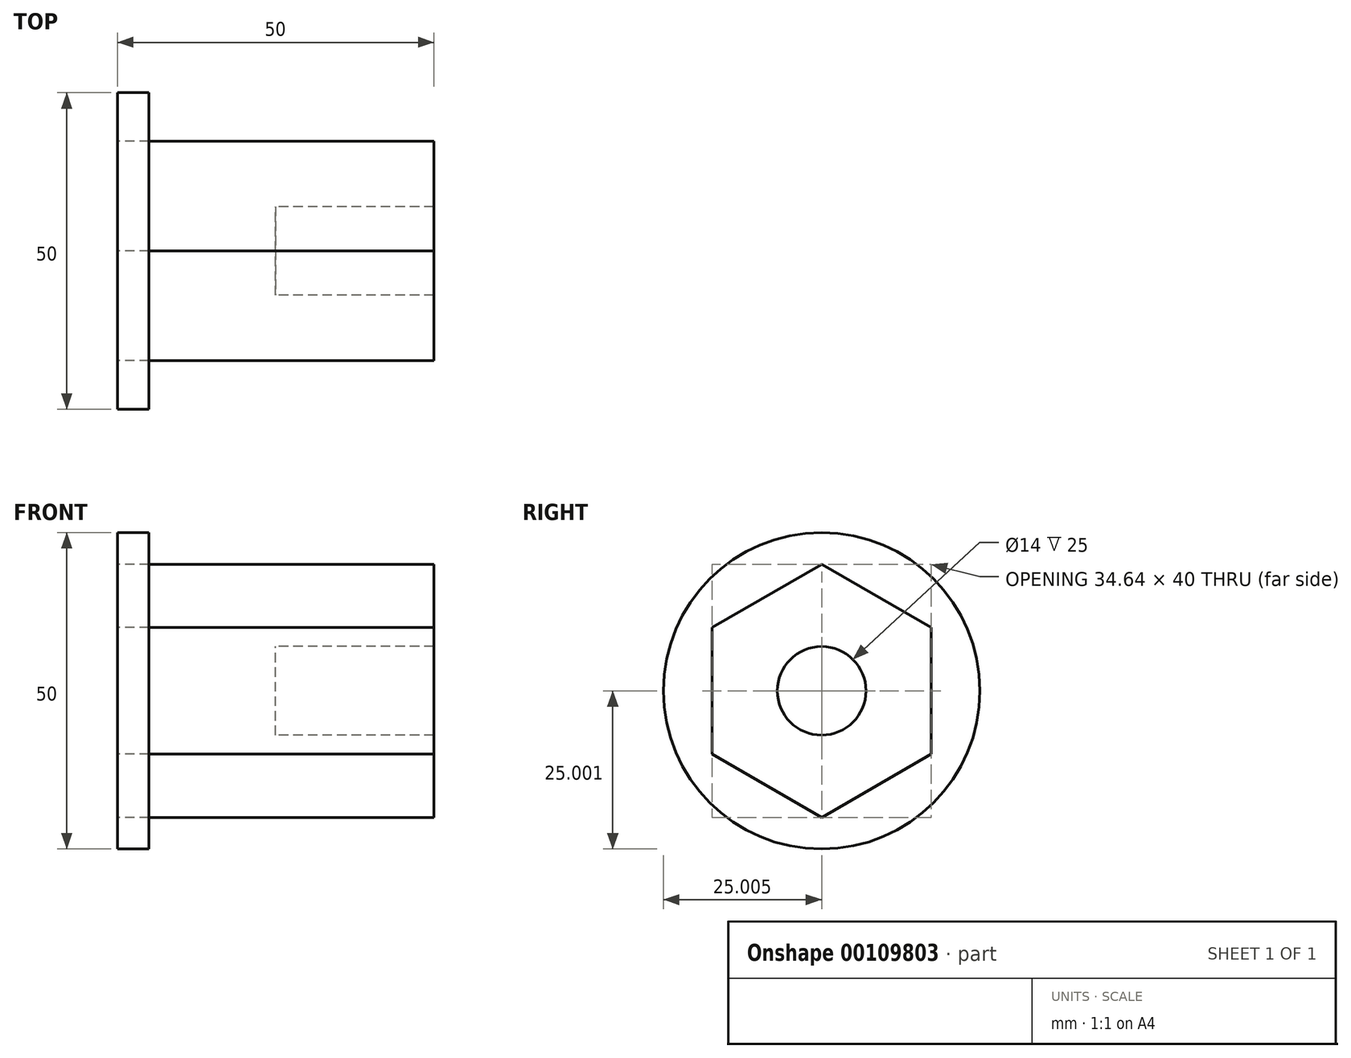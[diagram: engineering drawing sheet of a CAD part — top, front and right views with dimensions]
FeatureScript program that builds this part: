
annotation { "Feature Type Name" : "Feature", "Feature Type Description" : "" }
export const myFeature = defineFeature(function(context is Context, id is Id, definition is map)
    precondition{}
    {
        {
            var Q0;
            Q0=qCreatedBy(makeId("Right.planeOp"),FACE);
            var sketch = newSketch(context, id + "F0", { "sketchPlane" : qUnion([Q0])});
            skLineSegment(sketch, "E0", {"start": v(-258.27, -19.33) * mm, "end": v(-8.74, -19.33) * mm});
            skLineSegment(sketch, "E1", {"start": v(11.1, 3.15) * mm, "end": v(-12.25, 190) * mm});
            skLineSegment(sketch, "E2", {"start": v(-12.25, 190) * mm, "end": v(327.44, 461.76) * mm});
            skLineSegment(sketch, "E3", {"start": v(-148.68, -349.33) * mm, "end": v(-630.63, -349.33) * mm});
            skLineSegment(sketch, "E4", {"start": v(-18.68, -199.33) * mm, "end": v(-121.84, -199.33) * mm});
            skLineSegment(sketch, "E5", {"start": v(11.58, 180.67) * mm, "end": v(241.26, 180.67) * mm});
            skLineSegment(sketch, "E6", {"start": v(261.1, 203.15) * mm, "end": v(241.73, 358.2) * mm});
            skLineSegment(sketch, "E7", {"start": v(261.58, 380.67) * mm, "end": v(392.26, 380.67) * mm});
            skLineSegment(sketch, "E8", {"start": v(-148.68, -189.33) * mm, "end": v(-148.68, -349.33) * mm});
            skLineSegment(sketch, "E9", {"start": v(-290, -189.33) * mm, "end": v(-290, -119.33) * mm});
            skLineSegment(sketch, "E10", {"start": v(-121.84, -169.33) * mm, "end": v(-258.27, -169.33) * mm});
            skLineSegment(sketch, "E11", {"start": v(-148.68, -189.33) * mm, "end": v(-290, -189.33) * mm});
            skLineSegment(sketch, "E12", {"start": v(-258.27, -169.33) * mm, "end": v(-258.27, -19.33) * mm});
            skLineSegment(sketch, "E13", {"start": v(260.59, 545.38) * mm, "end": v(630.63, 82.5) * mm});
            skLineSegment(sketch, "E14", {"start": v(-630.63, 87.12) * mm, "end": v(-630.63, -443.05) * mm});
            skArc(sketch, "E15", {"start": v(-8.74, -19.33) * mm, "mid": v(6.26, -12.56) * mm, "end": v(11.1, 3.15) * mm});
            skArc(sketch, "E16", {"start": v(11.58, 180.67) * mm, "mid": v(-3.42, 173.9) * mm, "end": v(-8.27, 158.2) * mm});
            skArc(sketch, "E17", {"start": v(241.26, 180.67) * mm, "mid": v(256.26, 187.44) * mm, "end": v(261.1, 203.15) * mm});
            skArc(sketch, "E18", {"start": v(261.58, 380.67) * mm, "mid": v(246.58, 373.9) * mm, "end": v(241.73, 358.2) * mm});
            skLineSegment(sketch, "E19", {"start": v(-148.68, -349.33) * mm, "end": v(592.58, -349.33) * mm});
            skLineSegment(sketch, "E20", {"start": v(168.82, -49.33) * mm, "end": v(592.58, -49.33) * mm});
            skLineSegment(sketch, "E21", {"start": v(592.58, 18.95) * mm, "end": v(592.58, -393.06) * mm});
            skLineSegment(sketch, "E22", {"start": v(-18.68, -199.33) * mm, "end": v(514.77, 227.43) * mm});
            skLineSegment(sketch, "E23", {"start": v(-148.68, -299.33) * mm, "end": v(-630.63, -299.33) * mm});
            skLineSegment(sketch, "E24", {"start": v(-121.84, -199.33) * mm, "end": v(-121.84, -169.33) * mm});
            skLineSegment(sketch, "E25", {"start": v(-290, -119.33) * mm, "end": v(-630.63, -119.33) * mm});
            skLineSegment(sketch, "E26", {"start": v(-258.27, -19.33) * mm, "end": v(-630.63, -19.33) * mm});
            skLineSegment(sketch, "E27", {"start": v(-258.27, -169.33) * mm, "end": v(-258.27, -189.33) * mm});
            skLineSegment(sketch, "E28", {"start": v(-148.68, -189.33) * mm, "end": v(-148.68, -169.33) * mm});
            skLineSegment(sketch, "E29", {"start": v(-258.27, -169.33) * mm, "end": v(-148.68, -189.33) * mm});
            skLineSegment(sketch, "E30", {"start": v(-148.68, -169.33) * mm, "end": v(-258.27, -189.33) * mm});
            skArc(sketch, "E31", {"start": v(-132.68, -239.33) * mm, "mid": v(-128.58, -229.43) * mm, "end": v(-118.68, -225.33) * mm});
            skLineSegment(sketch, "E32", {"start": v(-118.68, -225.33) * mm, "end": v(-25.68, -225.33) * mm});
            skArc(sketch, "E33", {"start": v(-25.68, -225.33) * mm, "mid": v(-20.73, -223.28) * mm, "end": v(-18.68, -218.33) * mm});
            skLineSegment(sketch, "E34", {"start": v(-18.68, -218.33) * mm, "end": v(-18.68, -209.33) * mm});
            skLineSegment(sketch, "E35", {"start": v(-18.68, -209.33) * mm, "end": v(-148.68, -209.33) * mm});
            skLineSegment(sketch, "E36", {"start": v(-148.68, -209.33) * mm, "end": v(-148.68, -339.33) * mm});
            skLineSegment(sketch, "E37", {"start": v(-148.68, -339.33) * mm, "end": v(-139.68, -339.33) * mm});
            skArc(sketch, "E38", {"start": v(-139.68, -339.33) * mm, "mid": v(-134.73, -337.28) * mm, "end": v(-132.68, -332.33) * mm});
            skLineSegment(sketch, "E39", {"start": v(-132.68, -332.33) * mm, "end": v(-132.68, -239.33) * mm});
            skLineSegment(sketch, "E40", {"start": v(122.07, -484.72) * mm, "end": v(142.07, -484.72) * mm});
            skLineSegment(sketch, "E41", {"start": v(142.07, -484.72) * mm, "end": v(142.07, -524.72) * mm});
            skLineSegment(sketch, "E42", {"start": v(142.07, -524.72) * mm, "end": v(122.07, -524.72) * mm});
            skLineSegment(sketch, "E43", {"start": v(122.07, -524.72) * mm, "end": v(122.07, -484.72) * mm});
            skLineSegment(sketch, "E44", {"start": v(122.07, -494.72) * mm, "end": v(142.07, -494.72) * mm});
            skLineSegment(sketch, "E45", {"start": v(122.07, -514.72) * mm, "end": v(142.07, -514.72) * mm});
            skEllipse(sketch, "E46", {"center": v(132.07, -489.72) * mm, "majorRadius": 10 * mm, "minorRadius": 5 * mm, "majorAxis": v(-1, 0)});
            skEllipse(sketch, "E47", {"center": v(132.07, -519.72) * mm, "majorRadius": 10 * mm, "minorRadius": 5 * mm, "majorAxis": v(-1, 0)});
            skEllipse(sketch, "E48", {"center": v(132.07, -504.72) * mm, "majorRadius": 10 * mm, "minorRadius": 10 * mm, "majorAxis": v(0, 1)});
            skLineSegment(sketch, "E49", {"start": v(142.07, -497.72) * mm, "end": v(148.92, -497.72) * mm});
            skLineSegment(sketch, "E50", {"start": v(142.07, -511.72) * mm, "end": v(148.92, -511.72) * mm});
            skLineSegment(sketch, "E51", {"start": v(148.92, -497.72) * mm, "end": v(148.92, -511.72) * mm});
            skLineSegment(sketch, "E52", {"start": v(117.07, -529.72) * mm, "end": v(122.07, -529.72) * mm});
            skLineSegment(sketch, "E53", {"start": v(122.07, -529.72) * mm, "end": v(122.07, -479.72) * mm});
            skLineSegment(sketch, "E54", {"start": v(122.07, -479.72) * mm, "end": v(117.07, -479.72) * mm});
            skLineSegment(sketch, "E55", {"start": v(117.07, -479.72) * mm, "end": v(117.07, -529.72) * mm});
            skCircle(sketch, "E56", {"center": v(246.23, -520.38) * mm, "radius": 7 * mm});
            skLineSegment(sketch, "E57", {"start": v(228.91, -510.38) * mm, "end": v(228.91, -530.38) * mm});
            skLineSegment(sketch, "E58", {"start": v(263.56, -510.38) * mm, "end": v(263.56, -530.38) * mm});
            skLineSegment(sketch, "E59", {"start": v(228.91, -510.38) * mm, "end": v(246.23, -500.38) * mm});
            skLineSegment(sketch, "E60", {"start": v(246.23, -500.38) * mm, "end": v(263.56, -510.38) * mm});
            skLineSegment(sketch, "E61", {"start": v(228.91, -530.38) * mm, "end": v(246.23, -540.38) * mm});
            skLineSegment(sketch, "E62", {"start": v(246.23, -540.38) * mm, "end": v(263.56, -530.38) * mm});
            skCircle(sketch, "E63", {"center": v(246.23, -520.38) * mm, "radius": 25 * mm});
            skLineSegment(sketch, "E64", {"start": v(-121.84, -199.33) * mm, "end": v(-121.84, -209.33) * mm});
            skLineSegment(sketch, "E65", {"start": v(-18.68, -199.33) * mm, "end": v(-18.68, -209.33) * mm});
            skSolve(sketch);
        }
        {
            var Q0;
            Q0=makeQuery(id+"F0.imprint","IMPRINT",FACE,{"disambiguationData":[TD([[makeQuery(id+"F0.imprint","IMPRINT",EDGE,{"derivedFrom":sQuery(id+"F0.wireOp",EDGE,"E56")}),-1.0]])]});
            extrude(context, id + "F1", {"entities" : qUnion([Q0]), "depth" : 50 * mm});
        }
        {
            var Q0;
            Q0=makeQuery(id+"F0.imprint","IMPRINT",FACE,{"disambiguationData":[TD([[makeQuery(id+"F0.imprint","IMPRINT",EDGE,{"derivedFrom":sQuery(id+"F0.wireOp",EDGE,"E56")}),1.0]])]});
            extrude(context, id + "F2", {"entities" : qUnion([Q0]), "operationType" : NewBodyOperationType.ADD, "depth" : 25 * mm});
        }
        {
            var Q0;
            Q0=makeQuery(id+"F0.imprint","IMPRINT",FACE,{"disambiguationData":[TD([[makeQuery(id+"F0.imprint","IMPRINT",EDGE,{"derivedFrom":sQuery(id+"F0.wireOp",EDGE,"E57")}),-1.0]])]});
            extrude(context, id + "F3", {"entities" : qUnion([Q0]), "depth" : 5 * mm});
        }
    });
